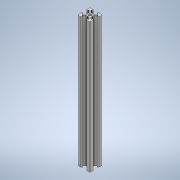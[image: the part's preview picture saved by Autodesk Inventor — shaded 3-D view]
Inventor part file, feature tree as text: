
AUTODESK INVENTOR PART (.ipt)
format: ipt  version: 2020 (Build 240168000, 168)  size: 274,944 bytes
history: native  units: mm
features: other x1, extrude x1, sketch x1
ambient origin geometry x8: Origin, YZ Plane, XZ Plane, XY Plane, X Axis, Y Axis, Z Axis, Center Point
bodies: Body1 (feature_tree)
feature tree (3):
  other  "Твердое тело1"
  extrude  "Выдавливание1"  Depth=0.25mm
  sketch  "Эскиз1"
